# Revit family: Toilet_Paper_Holder-Grohe-Defined-40974_Series
name_source: partatom
category: Specialty Equipment
units: mm (PartAtom-declared; Revit-internal decimal feet)

## family parameters
Cut with Voids When Loaded = No
Host = Face
OmniClass Number = 23.40.20.21.21
OmniClass Title = Toilet Paper Dispensers
Part Type = Normal
Room Calculation Point = No
Round Connector Dimension = Use Diameter
Shared = Yes

## types (2) — shared parameters
Assembly Code = C1030200
CalGreen Compliant = Yes
Default Elevation = 16"
Description = Paper Holder
Height = 5/8"
Installation Type = Wall Mounted
Length = 3 3/8"
Manufacturer = Grohe
Product Documentation Link = https://americanstandard.box.com
Product Page URL = https://www.grohe.us
Revised Date = 06/09/2023
URL = https://www.grohe.us
Width = 5 3/4"

## per-type parameters (varying)
| type | Finish | Material | Model |
| 40974000 | Metal-Grohe-000-Starlight Chrome | Metal-Grohe-000-Starlight Chrome | 40974000 |
| 40972EN0 | Metal-Grohe-EN0-Brushed Nickel | Metal-Grohe-EN0-Brushed Nickel | 40974EN0 |

## geometry (parser evidence)
native form markers: Sweep x5
no freeform markers — native parametric forms only
